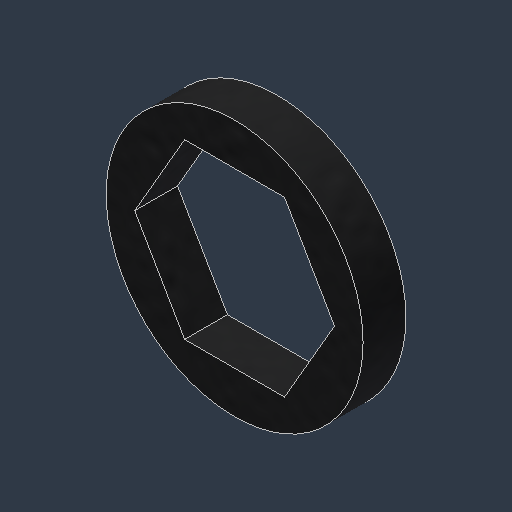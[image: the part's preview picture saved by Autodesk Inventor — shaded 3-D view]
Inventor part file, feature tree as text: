
AUTODESK INVENTOR PART (.ipt)
format: ipt  version: 2024.3 (Build 283343000, 343)  size: 103,424 bytes
history: native  units: mm (DEFAULTED — no unit token found)
features: extrude x1, sketch x1
ambient origin geometry x8: Origin, YZ Plane, XZ Plane, XY Plane, X Axis, Y Axis, Z Axis, Center Point
bodies: Solid1 (feature_tree)
feature tree (2):
  extrude  "Extrusion1"  Depth=3.175mm
  sketch  "Sketch2"  dims[d0=12.827mm d1=19.05mm d2=3.175mm d3=0.0mm]
